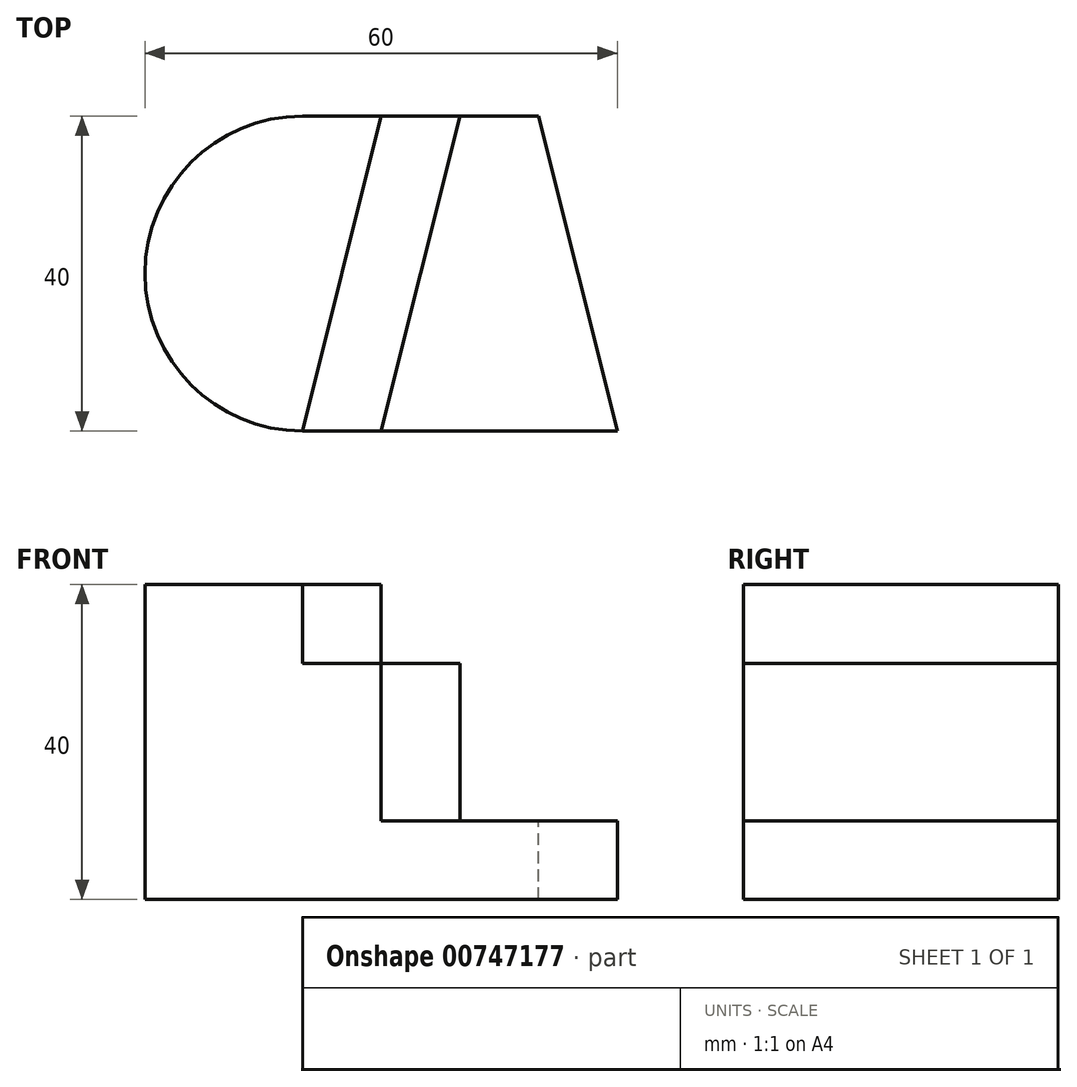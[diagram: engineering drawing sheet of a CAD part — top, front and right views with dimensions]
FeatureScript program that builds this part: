
annotation { "Feature Type Name" : "Feature", "Feature Type Description" : "" }
export const myFeature = defineFeature(function(context is Context, id is Id, definition is map)
    precondition{}
    {
        {
            var Q0;
            Q0=qCreatedBy(makeId("Front.planeOp"),FACE);
            var sketch = newSketch(context, id + "F0", { "sketchPlane" : qUnion([Q0])});
            skLineSegment(sketch, "E0", {"start": v(0, 0) * mm, "end": v(60, 0) * mm});
            skLineSegment(sketch, "E1", {"start": v(60, 0) * mm, "end": v(60, 10) * mm});
            skLineSegment(sketch, "E2", {"start": v(60, 10) * mm, "end": v(40, 10) * mm});
            skLineSegment(sketch, "E3", {"start": v(40, 10) * mm, "end": v(40, 30) * mm});
            skLineSegment(sketch, "E4", {"start": v(40, 30) * mm, "end": v(30, 30) * mm});
            skLineSegment(sketch, "E5", {"start": v(30, 30) * mm, "end": v(30, 40) * mm});
            skLineSegment(sketch, "E6", {"start": v(30, 40) * mm, "end": v(0, 40) * mm});
            skLineSegment(sketch, "E7", {"start": v(0, 40) * mm, "end": v(0, 0) * mm});
            skSolve(sketch);
        }
        {
            var Q0;
            Q0=makeQuery(id+"F0.imprint","IMPRINT",FACE,{"disambiguationData":[TD([[makeQuery(id+"F0.imprint","IMPRINT",EDGE,{"derivedFrom":sQuery(id+"F0.wireOp",EDGE,"E0")}),1.0]])]});
            extrude(context, id + "F1", {"entities" : qUnion([Q0]), "depth" : 40 * mm, "offsetDistance" : 25 * mm});
        }
        {
            var Q0;
            Q0=makeQuery(id+"F1.opExtrude","SWEPT_FACE",FACE,{"disambiguationData":[OSD([sQuery(id+"F0.wireOp",EDGE,"E4")])]});
            var sketch = newSketch(context, id + "F2", { "sketchPlane" : qUnion([Q0])});
            skLineSegment(sketch, "E8", {"start": v(40, 0) * mm, "end": v(30, -40) * mm});
            skLineSegment(sketch, "E9", {"start": v(30, -40) * mm, "end": v(40, -40) * mm});
            skLineSegment(sketch, "E10", {"start": v(40, -40) * mm, "end": v(40, 0) * mm});
            skSolve(sketch);
        }
        {
            var Q0;
            Q0=makeQuery(id+"F2.imprint","IMPRINT",FACE,{"disambiguationData":[TD([[makeQuery(id+"F2.imprint","IMPRINT",EDGE,{"derivedFrom":sQuery(id+"F2.wireOp",EDGE,"E8")}),1.0]])]});
            extrude(context, id + "F3", {"entities" : qUnion([Q0]), "operationType" : NewBodyOperationType.REMOVE, "oppositeDirection" : true, "depth" : 20 * mm, "offsetDistance" : 25 * mm});
        }
        {
            var Q0;
            Q0=makeQuery(id+"F3.boolean.opBoolean","MERGE",FACE,{"derivedFrom":[makeQuery(id+"F1.opExtrude","SWEPT_FACE",FACE,{"disambiguationData":[OSD([sQuery(id+"F0.wireOp",EDGE,"E2")])]}),makeQuery(id+"F3.opExtrude","CAP_FACE",FACE,{"disambiguationData":[OSD([sQuery(id+"F2.wireOp",EDGE,"E8"),sQuery(id+"F2.wireOp",EDGE,"E9"),sQuery(id+"F2.wireOp",EDGE,"E10")])],"isStart":false})]});
            var sketch = newSketch(context, id + "F4", { "sketchPlane" : qUnion([Q0])});
            skLineSegment(sketch, "E11", {"start": v(40, 0) * mm, "end": v(50, 0) * mm});
            skLineSegment(sketch, "E12", {"start": v(50, 0) * mm, "end": v(60, -40) * mm});
            skLineSegment(sketch, "E13", {"start": v(60, -40) * mm, "end": v(60, 0) * mm});
            skLineSegment(sketch, "E14", {"start": v(60, 0) * mm, "end": v(50, 0) * mm});
            skSolve(sketch);
        }
        {
            var Q0;
            Q0=makeQuery(id+"F4.imprint","IMPRINT",FACE,{"disambiguationData":[TD([[makeQuery(id+"F4.imprint","IMPRINT",EDGE,{"derivedFrom":sQuery(id+"F4.wireOp",EDGE,"E12")}),1.0]])]});
            extrude(context, id + "F5", {"entities" : qUnion([Q0]), "operationType" : NewBodyOperationType.REMOVE, "oppositeDirection" : true, "depth" : 10 * mm, "offsetDistance" : 25 * mm});
        }
        {
            var Q0;
            Q0=makeQuery(id+"F1.opExtrude","SWEPT_FACE",FACE,{"disambiguationData":[OSD([sQuery(id+"F0.wireOp",EDGE,"E6")])]});
            var sketch = newSketch(context, id + "F6", { "sketchPlane" : qUnion([Q0])});
            skLineSegment(sketch, "E15", {"start": v(30, 0) * mm, "end": v(30, -40) * mm});
            skLineSegment(sketch, "E16", {"start": v(30, -40) * mm, "end": v(20, -40) * mm});
            skLineSegment(sketch, "E17", {"start": v(20, -40) * mm, "end": v(30, 0) * mm});
            skSolve(sketch);
        }
        {
            var Q0;
            Q0=makeQuery(id+"F6.imprint","IMPRINT",FACE,{"disambiguationData":[TD([[makeQuery(id+"F6.imprint","IMPRINT",EDGE,{"derivedFrom":sQuery(id+"F6.wireOp",EDGE,"E15")}),1.0]])]});
            extrude(context, id + "F7", {"entities" : qUnion([Q0]), "operationType" : NewBodyOperationType.REMOVE, "oppositeDirection" : true, "depth" : 10 * mm, "offsetDistance" : 25 * mm});
        }
        {
            var Q0;
            Q0=makeQuery(id+"F1.opExtrude","SWEPT_FACE",FACE,{"disambiguationData":[OSD([sQuery(id+"F0.wireOp",EDGE,"E6")])]});
            var sketch = newSketch(context, id + "F8", { "sketchPlane" : qUnion([Q0])});
            skArc(sketch, "E18", {"start": v(20, 0) * mm, "mid": v(0, -20) * mm, "end": v(20, -40) * mm});
            skLineSegment(sketch, "E19", {"start": v(20, -40) * mm, "end": v(20, 0) * mm});
            skSolve(sketch);
        }
        {
            var Q0;
            {var subQ1=sQuery(id+"F0.wireOp",EDGE,"E6");var subQ2=makeQuery(id+"F1.opExtrude","CAP_EDGE",EDGE,{"disambiguationData":[OSD([subQ1])],"isStart":false});Q0=makeQuery(id+"F8.imprint","IMPRINT",FACE,{"disambiguationData":[TD([[makeQuery(id+"F8.imprint","IMPRINT",EDGE,{"derivedFrom":subQ2}),-1.0]])]});}
            var Q1;
            {var subQ0=sQuery(id+"F8.wireOp",EDGE,"E18");var subQ1=sQuery(id+"F0.wireOp",EDGE,"E6");var subQ2=makeQuery(id+"F1.opExtrude","CAP_EDGE",EDGE,{"disambiguationData":[OSD([subQ1])],"isStart":true});var subQ3=makeQuery(id+"F8.imprint","INTERSECT",VERTEX,{"derivedFrom":[subQ2,subQ0,sQuery(id+"F8.wireOp",EDGE,"E19")]});Q1=makeQuery(id+"F8.imprint","IMPRINT",FACE,{"disambiguationData":[TD([[makeQuery(id+"F8.imprint","IMPRINT",EDGE,{"disambiguationData":[TD([[subQ3,-1.0]])],"derivedFrom":subQ0}),-1.0]])]});}
            extrude(context, id + "F9", {"entities" : qUnion([Q0, Q1]), "operationType" : NewBodyOperationType.REMOVE, "oppositeDirection" : true, "depth" : 40 * mm, "offsetDistance" : 25 * mm});
        }
    });
